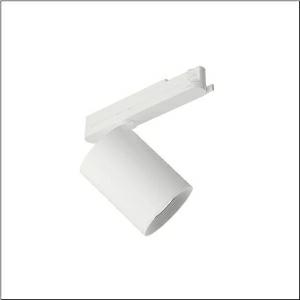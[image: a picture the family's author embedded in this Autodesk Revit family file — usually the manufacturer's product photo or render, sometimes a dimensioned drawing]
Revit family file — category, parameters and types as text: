
# Revit family: spot_11_51sd14ebb5a
name_source: partatom
category: Lighting Fixtures
units: mm (PartAtom-declared; Revit-internal decimal feet)

## family parameters
Cut with Voids When Loaded = No
Host = Face
Light Source = No
Part Type = Normal
Room Calculation Point = No
Round Connector Dimension = Use Diameter
Shared = No

## types (1)
- --- (1 x LED, 7340 lm, 51 W, 3000K)
    Apparent Load = 51 VA
    CIE Flux Codes = 95 98 100 100 100
    Color Rendering = 90
    Color Temperature = 3000K
    Default Elevation = 1800 mm
    Description = Spot 11, directional spotlight, light control with lens, of PMMA, LED rated luminous flux: 5.630lm, light colour: 930, control gear: ECG Multilumen, with 3-phase adapter, mains connection: 220..240V, AC, 50/60Hz, of aluminium, traffic white (RAL 9016), length: 253mm, diameter: 105mm, protection rating (complete): IP20, insulation class (complete): insulation class I (protective earthing), certification: CE, impact resistance: IK02, permissible ambient temperature for indoor applications: -20..+40°C, packaging unit: 1 piece
    Height = 175 mm
    Lamp = 1 x LED
    Lamp Light Flux = 7340 lm
    Lamp Power = 51 W
    Lamp count = 1
    Length = 105 mm
    Luminous efficacy = 144 lm/W
    Manufacturer = Siteco
    ModVariant = No
    Model = 51SD14EBB5A
    Mounting Place = Ceiling
    Mounting Type = Pendant
    Number of Poles = 1
    OnlyDefault = Yes
    Power Factor = 1
    Product Name = Spot 11
    Product group = directional spotlight
    ProductGroupID = 905
    Protection Class = Protection class I
    Protection Degree = IP 20
    RLX_Detail_Level = 1
    RLX_Emergency_Light_Flux = 0 lm
    RLX_Emergency_Type = 0
    RLX_Emergency_Type_DB = No
    RlxData = <blob elided: 17669 chars, md5=b256359e>
    Socket = socket
    Standby Power = 0 W
    System Light Flux = 7340 lm
    System Power = 51 W
    Type Comments = factory setting: luminous flux: 100 % | (ON | ON | ON | ON) | 1050 mA
    Type Image = l_1006697.jpg
    URL = http://relux.com
    VarID = @adj_168851
    Voltage = 0 V
    Weight = 0.00 kg
    Width = 0 mm  [stored 0 ft]

note: [stored X ft] marks values corroborated as IEEE doubles in the binary element streams (Revit-internal decimal feet)

## geometry (parser evidence)
native form markers: Blend x4, Sweep x10
no freeform markers — native parametric forms only
